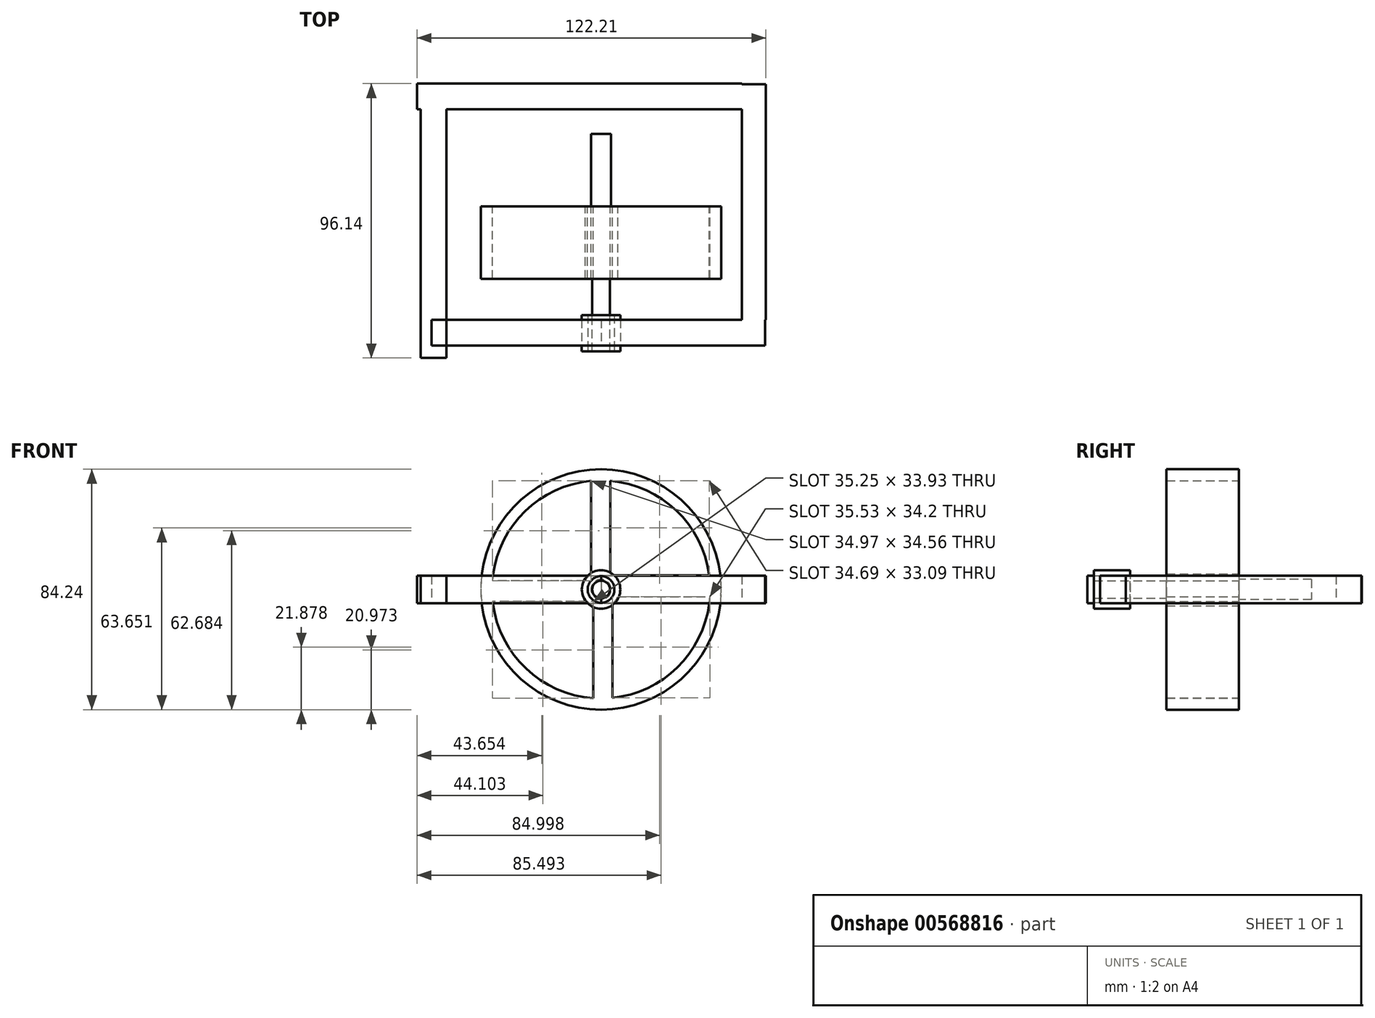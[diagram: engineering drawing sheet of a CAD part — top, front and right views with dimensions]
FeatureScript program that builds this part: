
annotation { "Feature Type Name" : "Feature", "Feature Type Description" : "" }
export const myFeature = defineFeature(function(context is Context, id is Id, definition is map)
    precondition{}
    {
        {
            var Q0;
            Q0=qCreatedBy(makeId("Front.planeOp"),FACE);
            var sketch = newSketch(context, id + "F0", { "sketchPlane" : qUnion([Q0])});
            skArc(sketch, "E0", {"start": v(3.93, 4.98) * mm, "mid": v(3.57, 5.25) * mm, "end": v(3.2, 5.49) * mm});
            skArc(sketch, "E1", {"start": v(-3.53, 38.05) * mm, "mid": v(-27.18, 26.86) * mm, "end": v(-38.09, 3.08) * mm});
            skCircle(sketch, "E2", {"center": v(0, 0) * mm, "radius": 42.12 * mm});
            skLineSegment(sketch, "E3", {"start": v(3.2, 5.49) * mm, "end": v(3.2, 38.08) * mm});
            skLineSegment(sketch, "E4", {"start": v(-3.53, 5.28) * mm, "end": v(-3.53, 38.05) * mm});
            skLineSegment(sketch, "E5", {"start": v(-4.78, -4.18) * mm, "end": v(-37.98, -4.18) * mm});
            skLineSegment(sketch, "E6", {"start": v(-5.55, 3.08) * mm, "end": v(-38.09, 3.08) * mm});
            skLineSegment(sketch, "E7", {"start": v(3.93, -4.98) * mm, "end": v(3.93, -38) * mm});
            skLineSegment(sketch, "E8", {"start": v(3.93, 4.98) * mm, "end": v(37.88, 4.98) * mm});
            skLineSegment(sketch, "E9", {"start": v(5.85, -2.47) * mm, "end": v(38.13, -2.47) * mm});
            skLineSegment(sketch, "E10", {"start": v(-2.73, -5.73) * mm, "end": v(-2.73, -38.11) * mm});
            skPoint(sketch, "E11.start.orphan", {"position": v(0, 6.35) * mm});
            skPoint(sketch, "E12.start.orphan", {"position": v(6.35, 0) * mm});
            skPoint(sketch, "E13.start.orphan", {"position": v(-6.35, 0) * mm});
            skPoint(sketch, "E14.start.orphan", {"position": v(0, -6.35) * mm});
            skArc(sketch, "E15.trimOffspring", {"start": v(37.88, 4.98) * mm, "mid": v(26.37, 27.65) * mm, "end": v(3.2, 38.08) * mm});
            skArc(sketch, "E16.trimOffspring", {"start": v(-37.98, -4.18) * mm, "mid": v(-26.5, -27.53) * mm, "end": v(-2.73, -38.11) * mm});
            skArc(sketch, "E17.trimOffspring", {"start": v(3.93, -38) * mm, "mid": v(27.53, -26.5) * mm, "end": v(38.13, -2.47) * mm});
            skArc(sketch, "E18.trimOffspring", {"start": v(-4.78, -4.18) * mm, "mid": v(-3.83, -5.06) * mm, "end": v(-2.73, -5.73) * mm});
            skArc(sketch, "E19.trimOffspring", {"start": v(3.93, -4.98) * mm, "mid": v(5.05, -3.85) * mm, "end": v(5.85, -2.47) * mm});
            skArc(sketch, "E20.trimOffspring", {"start": v(-3.53, 5.28) * mm, "mid": v(-4.67, 4.3) * mm, "end": v(-5.55, 3.08) * mm});
            skSolve(sketch);
        }
        {
            var Q0;
            Q0 = qSketchRegion(id + "F0", true);
            extrude(context, id + "F1", {"entities" : qUnion([Q0]), "depth" : 25.4 * mm, "offsetDistance" : 25.4 * mm});
        }
        {
            var Q0;
            Q0=makeQuery(id+"F1.opExtrude","CAP_FACE",FACE,{"disambiguationData":[OSD([sQuery(id+"F0.wireOp",EDGE,"E0"),sQuery(id+"F0.wireOp",EDGE,"E1"),sQuery(id+"F0.wireOp",EDGE,"E2"),sQuery(id+"F0.wireOp",EDGE,"E3"),sQuery(id+"F0.wireOp",EDGE,"E4"),sQuery(id+"F0.wireOp",EDGE,"E5"),sQuery(id+"F0.wireOp",EDGE,"E6"),sQuery(id+"F0.wireOp",EDGE,"E7"),sQuery(id+"F0.wireOp",EDGE,"E8"),sQuery(id+"F0.wireOp",EDGE,"E9"),sQuery(id+"F0.wireOp",EDGE,"E10"),sQuery(id+"F0.wireOp",EDGE,"E15.trimOffspring"),sQuery(id+"F0.wireOp",EDGE,"E16.trimOffspring"),sQuery(id+"F0.wireOp",EDGE,"E17.trimOffspring"),sQuery(id+"F0.wireOp",EDGE,"E18.trimOffspring"),sQuery(id+"F0.wireOp",EDGE,"E19.trimOffspring"),sQuery(id+"F0.wireOp",EDGE,"E20.trimOffspring")])],"isStart":false});
            var sketch = newSketch(context, id + "F2", { "sketchPlane" : qUnion([Q0])});
            skCircle(sketch, "E21", {"center": v(0, 0) * mm, "radius": 3.1 * mm});
            skSolve(sketch);
        }
        {
            var Q0;
            Q0 = qSketchRegion(id + "F2", true);
            extrude(context, id + "F3", {"entities" : qUnion([Q0]), "operationType" : NewBodyOperationType.ADD, "depth" : 25.4 * mm, "offsetDistance" : 25.4 * mm});
        }
        {
            var Q0;
            Q0=makeQuery(id+"F1.opExtrude","CAP_FACE",FACE,{"disambiguationData":[OSD([sQuery(id+"F0.wireOp",EDGE,"E0"),sQuery(id+"F0.wireOp",EDGE,"E1"),sQuery(id+"F0.wireOp",EDGE,"E2"),sQuery(id+"F0.wireOp",EDGE,"E3"),sQuery(id+"F0.wireOp",EDGE,"E4"),sQuery(id+"F0.wireOp",EDGE,"E5"),sQuery(id+"F0.wireOp",EDGE,"E6"),sQuery(id+"F0.wireOp",EDGE,"E7"),sQuery(id+"F0.wireOp",EDGE,"E8"),sQuery(id+"F0.wireOp",EDGE,"E9"),sQuery(id+"F0.wireOp",EDGE,"E10"),sQuery(id+"F0.wireOp",EDGE,"E15.trimOffspring"),sQuery(id+"F0.wireOp",EDGE,"E16.trimOffspring"),sQuery(id+"F0.wireOp",EDGE,"E17.trimOffspring"),sQuery(id+"F0.wireOp",EDGE,"E18.trimOffspring"),sQuery(id+"F0.wireOp",EDGE,"E19.trimOffspring"),sQuery(id+"F0.wireOp",EDGE,"E20.trimOffspring")])],"isStart":true});
            var sketch = newSketch(context, id + "F4", { "sketchPlane" : qUnion([Q0])});
            skCircle(sketch, "E22", {"center": v(0, 0) * mm, "radius": 3.53 * mm});
            skSolve(sketch);
        }
        {
            var Q0;
            Q0 = qSketchRegion(id + "F4", true);
            extrude(context, id + "F5", {"entities" : qUnion([Q0]), "operationType" : NewBodyOperationType.ADD, "depth" : 25.4 * mm, "offsetDistance" : 25.4 * mm});
        }
        {
            var Q0;
            Q0=makeQuery(id+"F3.opExtrude","CAP_FACE",FACE,{"disambiguationData":[OSD([sQuery(id+"F2.wireOp",EDGE,"E21")])],"isStart":false});
            var sketch = newSketch(context, id + "F6", { "sketchPlane" : qUnion([Q0])});
            skCircle(sketch, "E23", {"center": v(0, 0) * mm, "radius": 4.68 * mm});
            skCircle(sketch, "E24", {"center": v(0, 0) * mm, "radius": 6.75 * mm});
            skSolve(sketch);
        }
        {
            var Q0;
            Q0 = qSketchRegion(id + "F6", true);
            extrude(context, id + "F7", {"entities" : qUnion([Q0]), "oppositeDirection" : true, "depth" : 12.7 * mm, "offsetDistance" : 25.4 * mm});
        }
        {
            var Q0;
            Q0=qCreatedBy(makeId("Right.planeOp"),FACE);
            var sketch = newSketch(context, id + "F8", { "sketchPlane" : qUnion([Q0])});
            skLineSegment(sketch, "E25.bottom", {"start": v(-39.7, 4.81) * mm, "end": v(-48.73, 4.81) * mm});
            skLineSegment(sketch, "E25.top", {"start": v(-39.7, -4.81) * mm, "end": v(-48.73, -4.81) * mm});
            skLineSegment(sketch, "E25.left", {"start": v(-39.7, 4.81) * mm, "end": v(-39.7, -4.81) * mm});
            skLineSegment(sketch, "E25.right", {"start": v(-48.73, 4.81) * mm, "end": v(-48.73, -4.81) * mm});
            skPoint(sketch, "E25.middle", {"position": v(-44.22, 0) * mm});
            skSolve(sketch);
        }
        {
            var Q0;
            Q0 = qSketchRegion(id + "F8", true);
            extrude(context, id + "F9", {"entities" : qUnion([Q0]), "depth" : 57.4 * mm, "offsetDistance" : 25.4 * mm});
        }
        {
            var Q0;
            Q0=makeQuery(id+"F9.opExtrude","SWEPT_FACE",FACE,{"disambiguationData":[OSD([sQuery(id+"F8.wireOp",EDGE,"E25.left")])]});
            var sketch = newSketch(context, id + "F10", { "sketchPlane" : qUnion([Q0])});
            skLineSegment(sketch, "E26.bottom", {"start": v(-49.33, 4.81) * mm, "end": v(-57.75, 4.81) * mm});
            skLineSegment(sketch, "E26.top", {"start": v(-49.33, -4.81) * mm, "end": v(-57.75, -4.81) * mm});
            skLineSegment(sketch, "E26.left", {"start": v(-49.33, 4.81) * mm, "end": v(-49.33, -4.81) * mm});
            skLineSegment(sketch, "E26.right", {"start": v(-57.75, 4.81) * mm, "end": v(-57.75, -4.81) * mm});
            skPoint(sketch, "E26.middle", {"position": v(-53.54, 0) * mm});
            skSolve(sketch);
        }
        {
            var Q0;
            Q0 = qSketchRegion(id + "F10", true);
            extrude(context, id + "F11", {"entities" : qUnion([Q0]), "operationType" : NewBodyOperationType.ADD, "depth" : 82.55 * mm, "offsetDistance" : 25.4 * mm});
        }
        {
            var Q0;
            Q0=makeQuery(id+"F11.opExtrude","SWEPT_FACE",FACE,{"disambiguationData":[OSD([sQuery(id+"F10.wireOp",EDGE,"E26.left")])]});
            var sketch = newSketch(context, id + "F12", { "sketchPlane" : qUnion([Q0])});
            skLineSegment(sketch, "E27.bottom", {"start": v(-33.99, 4.81) * mm, "end": v(-43.01, 4.81) * mm});
            skLineSegment(sketch, "E27.top", {"start": v(-33.99, -4.81) * mm, "end": v(-43.01, -4.81) * mm});
            skLineSegment(sketch, "E27.left", {"start": v(-33.99, 4.81) * mm, "end": v(-33.99, -4.81) * mm});
            skLineSegment(sketch, "E27.right", {"start": v(-43.01, 4.81) * mm, "end": v(-43.01, -4.81) * mm});
            skPoint(sketch, "E27.middle", {"position": v(-38.5, 0) * mm});
            skSolve(sketch);
        }
        {
            var Q0;
            Q0 = qSketchRegion(id + "F12", true);
            extrude(context, id + "F13", {"entities" : qUnion([Q0]), "operationType" : NewBodyOperationType.ADD, "depth" : 113.8 * mm, "offsetDistance" : 25.4 * mm});
        }
        {
            var Q0;
            Q0=makeQuery(id+"F13.opExtrude","SWEPT_FACE",FACE,{"disambiguationData":[OSD([sQuery(id+"F12.wireOp",EDGE,"E27.left")])]});
            var sketch = newSketch(context, id + "F14", { "sketchPlane" : qUnion([Q0])});
            skLineSegment(sketch, "E28.bottom", {"start": v(-54.14, 4.81) * mm, "end": v(-63.17, 4.81) * mm});
            skLineSegment(sketch, "E28.top", {"start": v(-54.14, -4.81) * mm, "end": v(-63.17, -4.81) * mm});
            skLineSegment(sketch, "E28.left", {"start": v(-54.14, 4.81) * mm, "end": v(-54.14, -4.81) * mm});
            skLineSegment(sketch, "E28.right", {"start": v(-63.17, 4.81) * mm, "end": v(-63.17, -4.81) * mm});
            skPoint(sketch, "E28.middle", {"position": v(-58.65, 0) * mm});
            skSolve(sketch);
        }
        {
            var Q0;
            Q0 = qSketchRegion(id + "F14", true);
            extrude(context, id + "F15", {"entities" : qUnion([Q0]), "operationType" : NewBodyOperationType.ADD, "depth" : 87.12 * mm, "offsetDistance" : 25.4 * mm});
        }
        {
            var Q0;
            Q0 = qSketchRegion(id + "F8", true);
            extrude(context, id + "F16", {"entities" : qUnion([Q0]), "oppositeDirection" : true, "depth" : 59.44 * mm, "offsetDistance" : 25.4 * mm});
        }
    });
